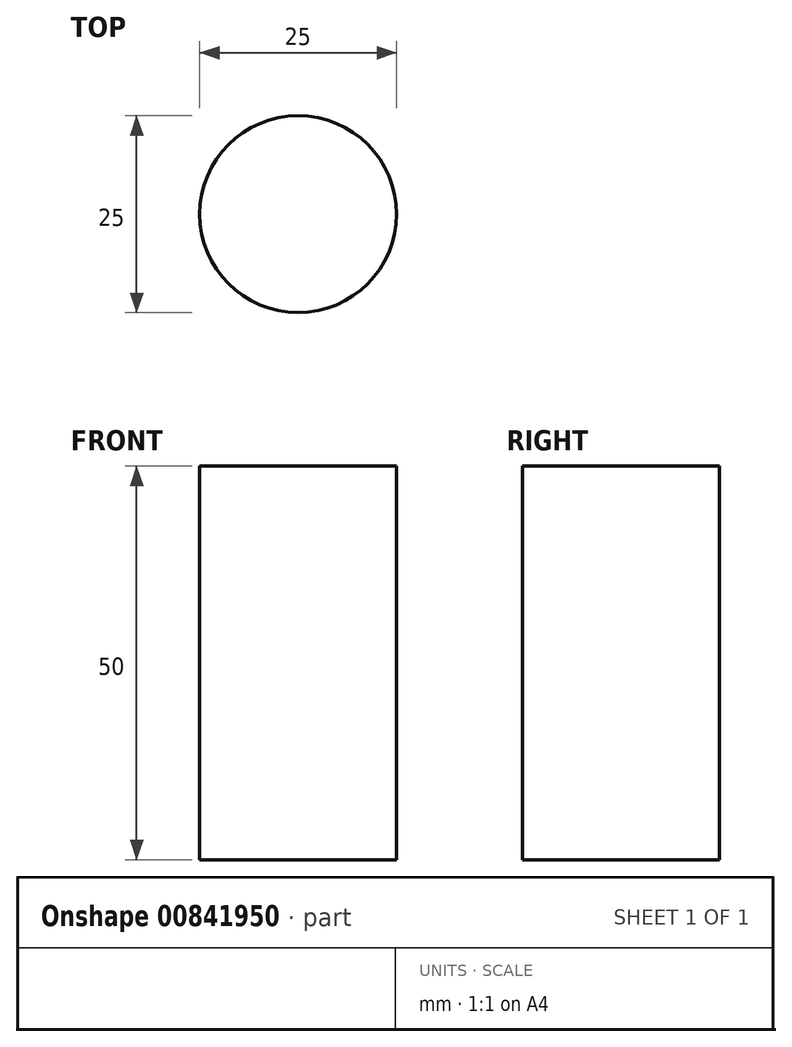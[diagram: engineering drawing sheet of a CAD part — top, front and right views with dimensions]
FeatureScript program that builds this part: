
annotation { "Feature Type Name" : "Feature", "Feature Type Description" : "" }
export const myFeature = defineFeature(function(context is Context, id is Id, definition is map)
    precondition{}
    {
        {
            var Q0;
            Q0=qCreatedBy(makeId("Top.planeOp"),FACE);
            var sketch = newSketch(context, id + "F0", { "sketchPlane" : qUnion([Q0])});
            skCircle(sketch, "E0", {"center": v(0, 0) * mm, "radius": 12.5 * mm});
            skSolve(sketch);
        }
        {
            var Q0;
            Q0 = qSketchRegion(id + "F0", true);
            extrude(context, id + "F1", {"entities" : qUnion([Q0]), "depth" : 50 * mm, "offsetDistance" : 25 * mm});
        }
    });
